# Revit family: Compact_Floodlights-CFL
name_source: partatom
category: Lighting Fixtures
revit_build: Autodesk Revit 2013 (Build: 20130531_2115(x64)
units: mm (PartAtom-declared; Revit-internal decimal feet)

## types (1)
- CFL
    Angle = 0.00°
    Apparent Load = 50 VA
    Assembly Code = D5020200
    Color Filter = 16777215
    Default Elevation = 0' - 0"
    Description = Exterior Lighting
    Dimming Lamp Color Temperature Shift = <None>
    Finish = All colors shall be a Super TGIC powder coat paint. Optional white (WH) and custom colors available.
    Full Load Current = 0 A
    Glass Material = Glass-Kim Lighting-Clear
    Initial Lumens = 810 lm
    Inside Material = Aluminum-Kim Lighting-Reflective_Finish
    Lamp = LED
    Light Angle = 60.00°
    Light Bulb = 1
    Light Bulb Visible = Yes
    Light Source-Kim Lighting = Light Source-Kim Lighting
    Manufacturer = KIM Lighting
    Manufacturer Fax = 626-369-2695
    MasterFormat Title = Flood Lighting
    Model = CFL
    Note Text = LF
    Note Visible = Yes
    Number of Poles = 1
    OmniClass Title = Lighting
    Outside Material = Metal-Kim Lighting-Bronze
    Photometric Notes = More IES files download in the Photometric Web link
    Photometric Web File = CFL-NF-213K50.IES
    Photometric Web Link = http://www.kimlighting.com
    Power Factor = 1
    Product Documentation Link = http://www.kimlighting.com
    Product Page URL = http://www.kimlighting.com
    Series = Compact Floodlight
    Tilt Angle = 60.00°
    URL = http://www.kimlighting.com
    Voltage = 120 V
    Wattage Comments = 26 & 35  Watt Compact Floodlight
    X = 2' - 1 27/32"
    Y = 0' - 7 3/16"

## geometry (parser evidence)
native form markers: Blend x12, Sweep x3
no freeform markers — native parametric forms only
